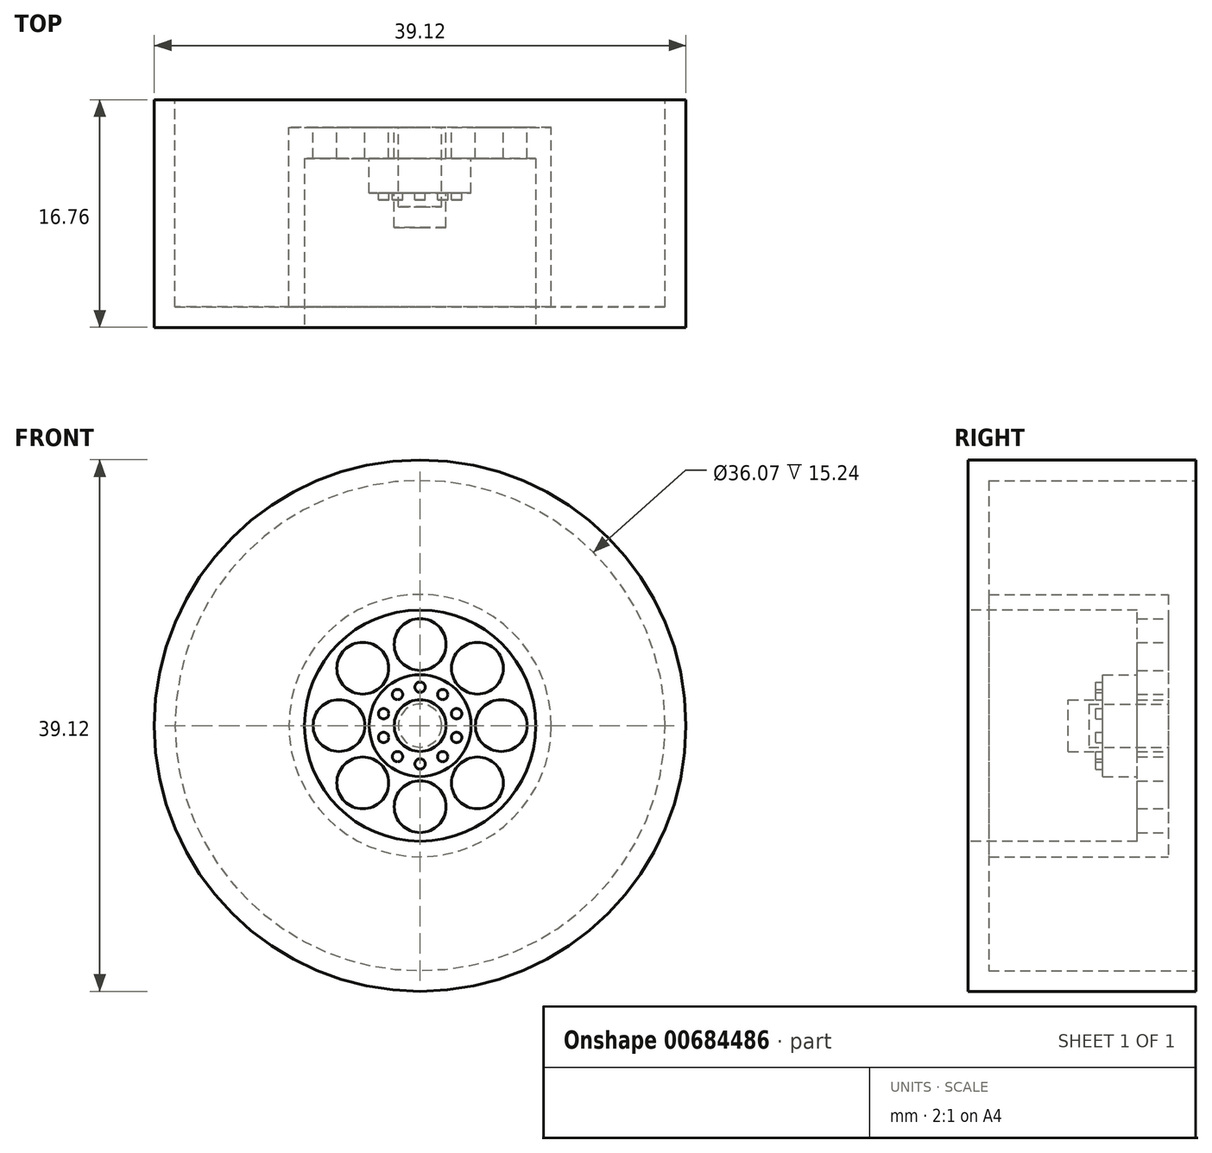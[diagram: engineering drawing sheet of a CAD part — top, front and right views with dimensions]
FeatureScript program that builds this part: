
annotation { "Feature Type Name" : "Feature", "Feature Type Description" : "" }
export const myFeature = defineFeature(function(context is Context, id is Id, definition is map)
    precondition{}
    {
        {
            var Q0;
            Q0=qCreatedBy(makeId("Front.planeOp"),FACE);
            var sketch = newSketch(context, id + "F0", { "sketchPlane" : qUnion([Q0])});
            skCircle(sketch, "E0", {"center": v(0, 0) * mm, "radius": 19.56 * mm});
            skSolve(sketch);
        }
        {
            var Q0;
            Q0 = qSketchRegion(id + "F0", true);
            extrude(context, id + "F1", {"entities" : qUnion([Q0]), "depth" : 16.76 * mm, "offsetDistance" : 25.4 * mm});
        }
        {
            var Q0;
            Q0=makeQuery(id+"F1.opExtrude","CAP_FACE",FACE,{"disambiguationData":[OSD([sQuery(id+"F0.wireOp",EDGE,"E0")])],"isStart":false});
            var sketch = newSketch(context, id + "F2", { "sketchPlane" : qUnion([Q0])});
            skCircle(sketch, "E1", {"center": v(0, 0) * mm, "radius": 8.5 * mm});
            skSolve(sketch);
        }
        {
            var Q0;
            Q0 = qSketchRegion(id + "F2", true);
            extrude(context, id + "F3", {"entities" : qUnion([Q0]), "operationType" : NewBodyOperationType.REMOVE, "oppositeDirection" : true, "depth" : 12.45 * mm, "offsetDistance" : 25.4 * mm});
        }
        {
            var Q0;
            Q0=makeQuery(id+"F1.opExtrude","CAP_FACE",FACE,{"disambiguationData":[OSD([sQuery(id+"F0.wireOp",EDGE,"E0")])],"isStart":true});
            var sketch = newSketch(context, id + "F4", { "sketchPlane" : qUnion([Q0])});
            skCircle(sketch, "E2", {"center": v(0, 0) * mm, "radius": 18.03 * mm});
            skCircle(sketch, "E3", {"center": v(0, 0) * mm, "radius": 9.65 * mm});
            skSolve(sketch);
        }
        {
            var Q0;
            Q0 = qSketchRegion(id + "F4", true);
            extrude(context, id + "F5", {"entities" : qUnion([Q0]), "operationType" : NewBodyOperationType.REMOVE, "oppositeDirection" : true, "depth" : 15.24 * mm, "offsetDistance" : 25.4 * mm});
        }
        {
            var Q0;
            Q0=makeQuery(id+"F5.boolean.opBoolean","SPLIT",FACE,{"disambiguationData":[TD([makeQuery(id+"F5.opExtrude","SWEPT_FACE",FACE,{"disambiguationData":[OSD([sQuery(id+"F4.wireOp",EDGE,"E3")])]})])],"derivedFrom":makeQuery(id+"F1.opExtrude","CAP_FACE",FACE,{"disambiguationData":[OSD([sQuery(id+"F0.wireOp",EDGE,"E0")])],"isStart":true})});
            var sketch = newSketch(context, id + "F6", { "sketchPlane" : qUnion([Q0])});
            skCircle(sketch, "E4", {"center": v(0, 0) * mm, "radius": 9.65 * mm});
            skSolve(sketch);
        }
        {
            var Q0;
            Q0 = qSketchRegion(id + "F6", true);
            extrude(context, id + "F7", {"entities" : qUnion([Q0]), "operationType" : NewBodyOperationType.REMOVE, "oppositeDirection" : true, "depth" : 2.03 * mm, "offsetDistance" : 25.4 * mm});
        }
        {
            var Q0;
            Q0=makeQuery(id+"F7.boolean.opBoolean","COPY",FACE,{"derivedFrom":makeQuery(id+"F7.opExtrude","CAP_FACE",FACE,{"disambiguationData":[OSD([sQuery(id+"F6.wireOp",EDGE,"E4")])],"isStart":false})});
            var sketch = newSketch(context, id + "F8", { "sketchPlane" : qUnion([Q0])});
            skCircle(sketch, "E5", {"center": v(0, 5.97) * mm, "radius": 1.9 * mm});
            skCircle(sketch, "E6.1.0", {"center": v(-4.22, 4.22) * mm, "radius": 1.9 * mm});
            skCircle(sketch, "E6.2.0", {"center": v(-5.97, 0) * mm, "radius": 1.9 * mm});
            skCircle(sketch, "E6.3.0", {"center": v(-4.22, -4.22) * mm, "radius": 1.9 * mm});
            skCircle(sketch, "E6.4.0", {"center": v(0, -5.97) * mm, "radius": 1.9 * mm});
            skCircle(sketch, "E6.5.0", {"center": v(4.22, -4.22) * mm, "radius": 1.9 * mm});
            skCircle(sketch, "E6.6.0", {"center": v(5.97, 0) * mm, "radius": 1.9 * mm});
            skCircle(sketch, "E6.7.0", {"center": v(4.22, 4.22) * mm, "radius": 1.9 * mm});
            skPoint(sketch, "E6.center", {"position": v(0, 0) * mm});
            skSolve(sketch);
        }
        {
            var Q0;
            Q0=makeQuery(id+"F8.imprint","IMPRINT",FACE,{"disambiguationData":[TD([[makeQuery(id+"F8.imprint","IMPRINT",EDGE,{"derivedFrom":sQuery(id+"F8.wireOp",EDGE,"E6.5.0")}),1.0]])]});
            var Q1;
            Q1=makeQuery(id+"F8.imprint","IMPRINT",FACE,{"disambiguationData":[TD([[makeQuery(id+"F8.imprint","IMPRINT",EDGE,{"derivedFrom":sQuery(id+"F8.wireOp",EDGE,"E6.6.0")}),1.0]])]});
            var Q2;
            Q2=makeQuery(id+"F8.imprint","IMPRINT",FACE,{"disambiguationData":[TD([[makeQuery(id+"F8.imprint","IMPRINT",EDGE,{"derivedFrom":sQuery(id+"F8.wireOp",EDGE,"E6.7.0")}),1.0]])]});
            var Q3;
            Q3=makeQuery(id+"F8.imprint","IMPRINT",FACE,{"disambiguationData":[TD([[makeQuery(id+"F8.imprint","IMPRINT",EDGE,{"derivedFrom":sQuery(id+"F8.wireOp",EDGE,"E5")}),1.0]])]});
            var Q4;
            Q4=makeQuery(id+"F8.imprint","IMPRINT",FACE,{"disambiguationData":[TD([[makeQuery(id+"F8.imprint","IMPRINT",EDGE,{"derivedFrom":sQuery(id+"F8.wireOp",EDGE,"E6.1.0")}),1.0]])]});
            var Q5;
            Q5=makeQuery(id+"F8.imprint","IMPRINT",FACE,{"disambiguationData":[TD([[makeQuery(id+"F8.imprint","IMPRINT",EDGE,{"derivedFrom":sQuery(id+"F8.wireOp",EDGE,"E6.2.0")}),1.0]])]});
            var Q6;
            Q6=makeQuery(id+"F8.imprint","IMPRINT",FACE,{"disambiguationData":[TD([[makeQuery(id+"F8.imprint","IMPRINT",EDGE,{"derivedFrom":sQuery(id+"F8.wireOp",EDGE,"E6.3.0")}),1.0]])]});
            var Q7;
            Q7=makeQuery(id+"F8.imprint","IMPRINT",FACE,{"disambiguationData":[TD([[makeQuery(id+"F8.imprint","IMPRINT",EDGE,{"derivedFrom":sQuery(id+"F8.wireOp",EDGE,"E6.4.0")}),1.0]])]});
            extrude(context, id + "F9", {"entities" : qUnion([Q0, Q1, Q2, Q3, Q4, Q5, Q6, Q7]), "operationType" : NewBodyOperationType.REMOVE, "oppositeDirection" : true, "depth" : 25.4 * mm, "offsetDistance" : 25.4 * mm});
        }
        {
            var Q0;
            Q0=makeQuery(id+"F3.boolean.opBoolean","COPY",FACE,{"derivedFrom":makeQuery(id+"F3.opExtrude","CAP_FACE",FACE,{"disambiguationData":[OSD([sQuery(id+"F2.wireOp",EDGE,"E1")])],"isStart":false})});
            var sketch = newSketch(context, id + "F10", { "sketchPlane" : qUnion([Q0])});
            skCircle(sketch, "E7", {"center": v(0, 0) * mm, "radius": 3.75 * mm});
            skCircle(sketch, "E8", {"center": v(0, 0) * mm, "radius": 1.9 * mm});
            skSolve(sketch);
        }
        {
            var Q0;
            Q0=makeQuery(id+"F10.imprint","IMPRINT",FACE,{"disambiguationData":[TD([[makeQuery(id+"F10.imprint","IMPRINT",EDGE,{"derivedFrom":sQuery(id+"F10.wireOp",EDGE,"E8")}),1.0]])]});
            extrude(context, id + "F11", {"entities" : qUnion([Q0]), "operationType" : NewBodyOperationType.ADD, "depth" : 5.08 * mm, "offsetDistance" : 25.4 * mm});
        }
        {
            var Q0;
            Q0 = qSketchRegion(id + "F10", true);
            extrude(context, id + "F12", {"entities" : qUnion([Q0]), "operationType" : NewBodyOperationType.ADD, "depth" : 2.54 * mm, "offsetDistance" : 25.4 * mm});
        }
        {
            var Q0;
            Q0=makeQuery(id+"F12.opExtrude","CAP_FACE",FACE,{"disambiguationData":[OSD([sQuery(id+"F10.wireOp",EDGE,"E7"),sQuery(id+"F10.wireOp",EDGE,"E8")])],"isStart":false});
            var sketch = newSketch(context, id + "F13", { "sketchPlane" : qUnion([Q0])});
            skCircle(sketch, "E9", {"center": v(0, 2.83) * mm, "radius": 0.38 * mm});
            skCircle(sketch, "E10.1.0", {"center": v(-1.66, 2.29) * mm, "radius": 0.38 * mm});
            skCircle(sketch, "E10.2.0", {"center": v(-2.69, 0.87) * mm, "radius": 0.38 * mm});
            skCircle(sketch, "E10.3.0", {"center": v(-2.69, -0.87) * mm, "radius": 0.38 * mm});
            skCircle(sketch, "E10.4.0", {"center": v(-1.66, -2.29) * mm, "radius": 0.38 * mm});
            skCircle(sketch, "E10.5.0", {"center": v(0, -2.83) * mm, "radius": 0.38 * mm});
            skCircle(sketch, "E10.6.0", {"center": v(1.66, -2.29) * mm, "radius": 0.38 * mm});
            skCircle(sketch, "E10.7.0", {"center": v(2.69, -0.87) * mm, "radius": 0.38 * mm});
            skCircle(sketch, "E10.8.0", {"center": v(2.69, 0.87) * mm, "radius": 0.38 * mm});
            skCircle(sketch, "E10.9.0", {"center": v(1.66, 2.29) * mm, "radius": 0.38 * mm});
            skPoint(sketch, "E10.center", {"position": v(0, 0) * mm});
            skSolve(sketch);
        }
        {
            var Q0;
            Q0 = qSketchRegion(id + "F13", true);
            extrude(context, id + "F14", {"entities" : qUnion([Q0]), "operationType" : NewBodyOperationType.ADD, "depth" : 0.5 * mm, "offsetDistance" : 25.4 * mm});
        }
        {
            var Q0;
            Q0=makeQuery(id+"F7.boolean.opBoolean","COPY",FACE,{"derivedFrom":makeQuery(id+"F7.opExtrude","CAP_FACE",FACE,{"disambiguationData":[OSD([sQuery(id+"F6.wireOp",EDGE,"E4")])],"isStart":false})});
            var sketch = newSketch(context, id + "F15", { "sketchPlane" : qUnion([Q0])});
            skCircle(sketch, "E11", {"center": v(0, 0) * mm, "radius": 1.59 * mm});
            skSolve(sketch);
        }
        {
            var Q0;
            Q0 = qSketchRegion(id + "F15", true);
            extrude(context, id + "F16", {"entities" : qUnion([Q0]), "operationType" : NewBodyOperationType.REMOVE, "oppositeDirection" : true, "depth" : 5.87 * mm, "offsetDistance" : 25.4 * mm});
        }
    });
